# Revit family: Basin-Wall_Hung-Sloan-SS-3145
name_source: partatom
category: Plumbing Fixtures
revit_build: Autodesk Revit 2014 (Build: 20130308_1515(x64)
units: mm (PartAtom-declared; Revit-internal decimal feet)

## types (1)
- SS-3145
    ADA Compliant = Yes
    Assembly Code = D2010300
    Basin Shape = Triangular
    CW Connection = Yes
    CWFU = 1.5
    Cold Water Connection Diameter = 1/2"
    Cold Water Connection Radius = 1/4"
    Default Elevation = 29 1/16"
    Description = Wall Mounted Corner Lavatory, 16-1/2” x 4-1/2”, Single hole
    HW Connection = Yes
    HWFU = 1.5
    Height = 6 1/16"
    Hot Water Connection Diameter = 1/2"
    Hot Water Connection Radius = 1/4"
    IAPMO Compliance = cUPC
    Installation Type = Wall Mounted
    Length = 6 1/2"
    Manufacturer = SLOAN
    Material = Vitreous China-Sloan-White
    Model = SS-3145
    Price = Prices may vary. Please consult Manufacturer Representative for most up-to-date price list.
    URL = https://www.sloan.com
    Vent Connection = No
    WFU = 2
    Warranty Information = 3 Years
    Waste Connection = Yes
    Waste Connection Diameter = 1 1/4"
    Waste Connection Radius = 5/8"
    Width = 16 1/2"

## geometry (parser evidence)
native form markers: Sweep x3
no freeform markers — native parametric forms only
